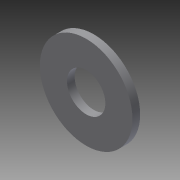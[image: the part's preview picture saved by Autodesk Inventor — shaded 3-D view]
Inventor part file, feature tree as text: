
AUTODESK INVENTOR PART (.ipt)
format: ipt  version: 2014 SP2 (Build 180246200, 246)  size: 91,136 bytes
history: native  units: in
note: dims shown in document units (in); Inventor stores cm internally (conversion verified against a paired STEP export)
features: other x7, extrude x1, sketch x1
ambient origin geometry x8: Origin, YZ Plane, XZ Plane, XY Plane, X Axis, Y Axis, Z Axis, Center Point
bodies: Solid1 (feature_tree)
feature tree (9):
  extrude  "Extrusion1"  TaperAngle=0.0deg  [1 undecoded]
  other  "to_a_XY"
  other  "to_a_YZ"
  other  "to_a_ZX"
  other  "to_a_X"
  other  "to_a_Y"
  other  "to_a_Z"
  other  "to_a_Center"
  sketch  "Sketch_1"  dims[d0=0.065in d1=0.0in d2=0.0in]
note: 1 required parameter value undecoded (feature->parameter linkage not recoverable at this tier; creation-order binding heuristic only, values carry confidence <= 0.55)
